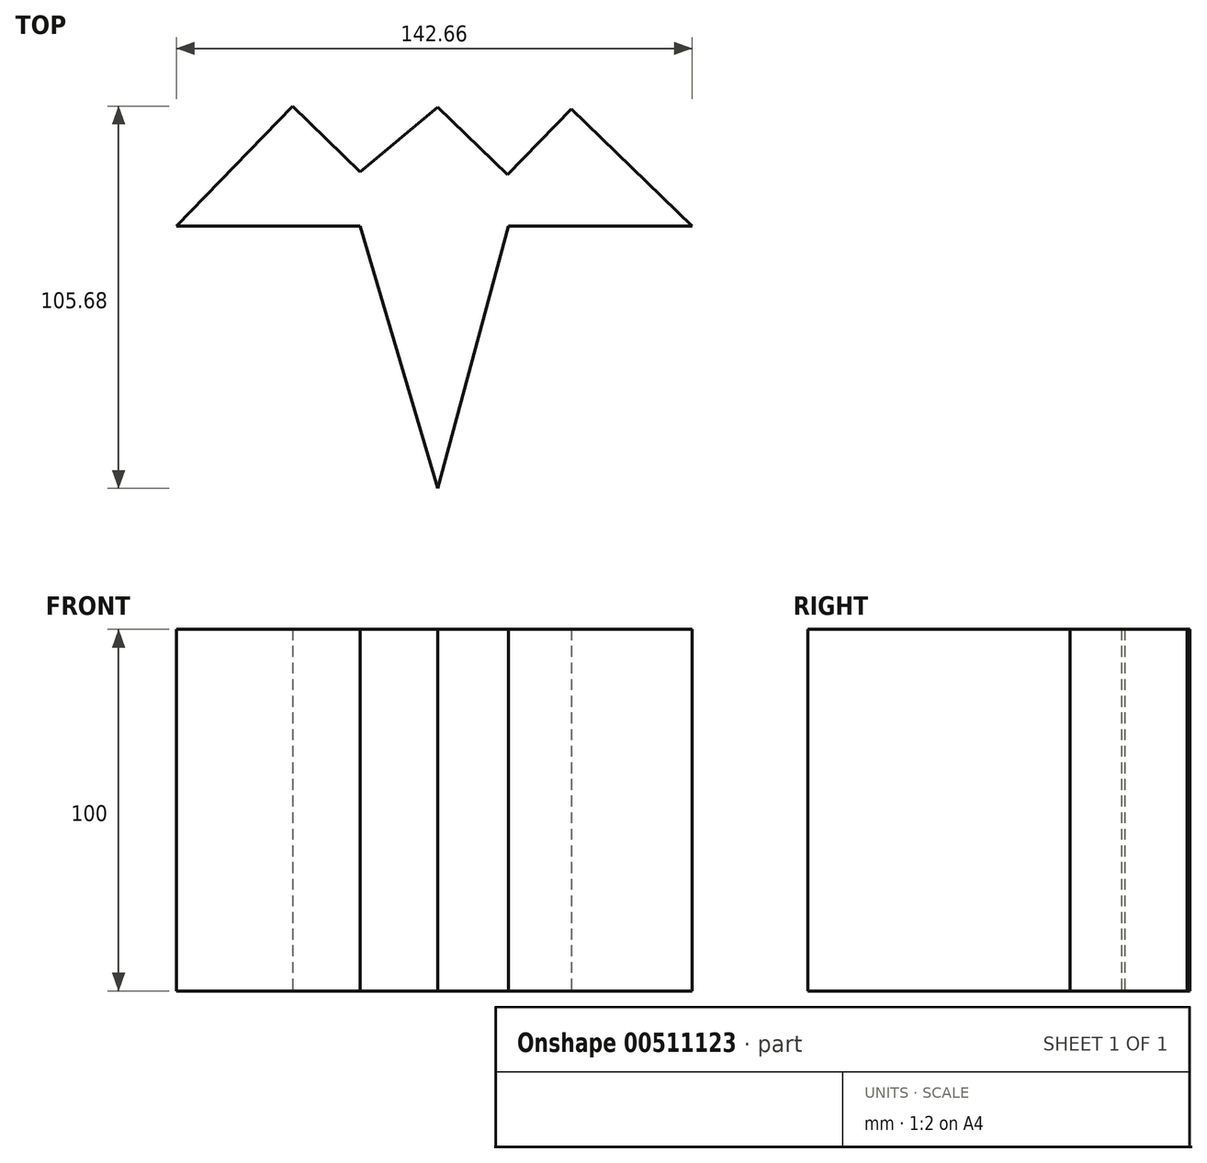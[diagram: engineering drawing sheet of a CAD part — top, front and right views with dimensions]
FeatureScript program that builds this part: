
annotation { "Feature Type Name" : "Feature", "Feature Type Description" : "" }
export const myFeature = defineFeature(function(context is Context, id is Id, definition is map)
    precondition{}
    {
        {
            var Q0;
            Q0=qCreatedBy(makeId("Top.planeOp"),FACE);
            var sketch = newSketch(context, id + "F0", { "sketchPlane" : qUnion([Q0])});
            skLineSegment(sketch, "E0", {"start": v(0, 46.73) * mm, "end": v(19.3, 28.04) * mm});
            skLineSegment(sketch, "E1", {"start": v(19.3, 28.04) * mm, "end": v(36.94, 46.25) * mm});
            skLineSegment(sketch, "E2", {"start": v(36.94, 46.25) * mm, "end": v(70.4, 13.85) * mm});
            skLineSegment(sketch, "E3", {"start": v(70.4, 13.85) * mm, "end": v(19.6, 13.85) * mm});
            skLineSegment(sketch, "E4", {"start": v(19.6, 13.85) * mm, "end": v(0, -58.68) * mm});
            skLineSegment(sketch, "E5", {"start": v(0, -58.68) * mm, "end": v(-21.45, 13.85) * mm});
            skLineSegment(sketch, "E6", {"start": v(-21.45, 13.85) * mm, "end": v(-72.25, 13.85) * mm});
            skLineSegment(sketch, "E7", {"start": v(-72.25, 13.85) * mm, "end": v(-40.15, 47) * mm});
            skLineSegment(sketch, "E8", {"start": v(-40.15, 47) * mm, "end": v(-21.45, 28.9) * mm});
            skLineSegment(sketch, "E9", {"start": v(-21.45, 28.9) * mm, "end": v(0, 46.73) * mm});
            skSolve(sketch);
        }
        {
            var Q0;
            Q0=makeQuery(id+"F0.imprint","IMPRINT",FACE,{"disambiguationData":[TD([[makeQuery(id+"F0.imprint","IMPRINT",EDGE,{"derivedFrom":sQuery(id+"F0.wireOp",EDGE,"E0")}),-1.0]])]});
            extrude(context, id + "F1", {"entities" : qUnion([Q0]), "depth" : 100 * mm});
        }
    });
